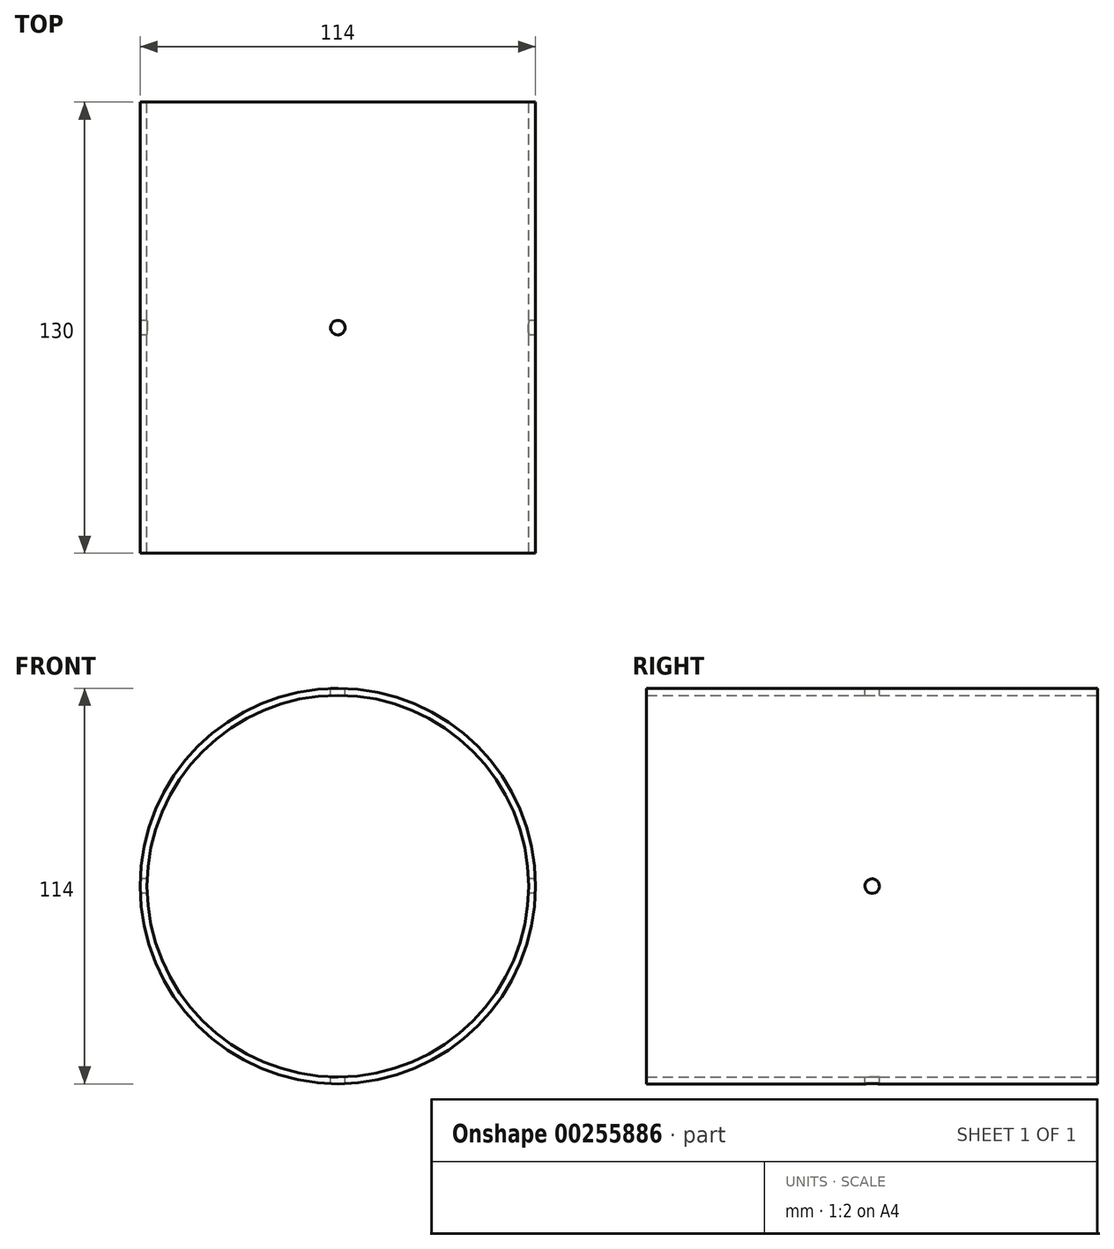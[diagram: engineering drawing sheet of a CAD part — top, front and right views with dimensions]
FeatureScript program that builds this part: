
annotation { "Feature Type Name" : "Feature", "Feature Type Description" : "" }
export const myFeature = defineFeature(function(context is Context, id is Id, definition is map)
    precondition{}
    {
        {
            var Q0;
            Q0=qCreatedBy(makeId("Front.planeOp"),FACE);
            var sketch = newSketch(context, id + "F0", { "sketchPlane" : qUnion([Q0])});
            skCircle(sketch, "E0", {"center": v(11.2, 9.37) * mm, "radius": 57 * mm});
            skCircle(sketch, "E1.0", {"center": v(11.2, 9.37) * mm, "radius": 55 * mm});
            skLineSegment(sketch, "E2", {"start": v(11.2, 9.37) * mm, "end": v(-33.3, 41.7) * mm, "construction": true});
            skLineSegment(sketch, "E3", {"start": v(11.2, 9.37) * mm, "end": v(-5.8, 61.68) * mm, "construction": true});
            skLineSegment(sketch, "E4", {"start": v(11.2, 9.37) * mm, "end": v(28.2, 61.68) * mm, "construction": true});
            skPoint(sketch, "E5.start.orphan", {"position": v(11.2, -45.63) * mm});
            skPoint(sketch, "E6.start.orphan", {"position": v(-43.8, 9.37) * mm});
            skLineSegment(sketch, "E7", {"start": v(-43.8, 9.37) * mm, "end": v(11.2, 9.37) * mm, "construction": true});
            skLineSegment(sketch, "E8", {"start": v(11.2, 9.37) * mm, "end": v(55.7, 41.7) * mm, "construction": true});
            skLineSegment(sketch, "E9", {"start": v(11.2, 9.37) * mm, "end": v(66.2, 9.37) * mm, "construction": true});
            skLineSegment(sketch, "E10", {"start": v(11.2, 9.37) * mm, "end": v(55.7, -22.96) * mm, "construction": true});
            skLineSegment(sketch, "E11", {"start": v(11.2, 9.37) * mm, "end": v(28.2, -42.94) * mm, "construction": true});
            skLineSegment(sketch, "E12", {"start": v(11.2, 9.37) * mm, "end": v(-5.8, -42.94) * mm, "construction": true});
            skLineSegment(sketch, "E13", {"start": v(11.2, 9.37) * mm, "end": v(-33.3, -22.96) * mm, "construction": true});
            skSolve(sketch);
        }
        {
            var Q0;
            Q0 = qSketchRegion(id + "F0", true);
            extrude(context, id + "F1", {"entities" : qUnion([Q0]), "depth" : 130 * mm, "symmetric" : true});
        }
        {
            var Q0;
            Q0=qCreatedBy(makeId("Right.planeOp"),FACE);
            var Q1;
            Q1=sQuery(id+"F0.wireOp",VERTEX,"E11.start");
            cPlane(context, id + "F2", {"entities" : qUnion([Q0, Q1]), "cplaneType" : CPlaneType.PLANE_POINT, "offset" : 25 * mm, "width" : 150 * mm, "height" : 150 * mm});
        }
        {
            var Q0;
            Q0=qCreatedBy(id+"F2.planeOp",FACE);
            var sketch = newSketch(context, id + "F3", { "sketchPlane" : qUnion([Q0])});
            skCircle(sketch, "E14", {"center": v(0, 9.37) * mm, "radius": 2.1 * mm});
            skSolve(sketch);
        }
        {
            var Q0;
            Q0=makeQuery(id+"F3.imprint","IMPRINT",FACE,{"disambiguationData":[TD([[makeQuery(id+"F3.imprint","IMPRINT",EDGE,{"derivedFrom":sQuery(id+"F3.wireOp",EDGE,"E14")}),1.0]])]});
            var Q1;
            Q1=sQuery(id+"F3.wireOp",EDGE,"E14");
            extrude(context, id + "F4", {"entities" : qUnion([Q0]), "operationType" : NewBodyOperationType.REMOVE, "surfaceEntities" : qUnion([Q1]), "depth" : 140 * mm, "symmetric" : true});
        }
        {
            var Q0;
            Q0=qCreatedBy(makeId("Top.planeOp"),FACE);
            var sketch = newSketch(context, id + "F5", { "sketchPlane" : qUnion([Q0])});
            skCircle(sketch, "E15", {"center": v(11.2, 0) * mm, "radius": 2.1 * mm});
            skSolve(sketch);
        }
        {
            var Q0;
            Q0=makeQuery(id+"F5.imprint","IMPRINT",FACE,{"disambiguationData":[TD([[makeQuery(id+"F5.imprint","IMPRINT",EDGE,{"derivedFrom":sQuery(id+"F5.wireOp",EDGE,"E15")}),1.0]])]});
            extrude(context, id + "F6", {"entities" : qUnion([Q0]), "operationType" : NewBodyOperationType.REMOVE, "oppositeDirection" : true, "depth" : 200 * mm, "symmetric" : true});
        }
    });
